# Revit family: Faucet-Kitchen-KOHLER-Ealing-K-R28702_1
name_source: partatom
category: Plumbing Fixtures
units: mm (PartAtom-declared; Revit-internal decimal feet)

## family parameters
Cut with Voids When Loaded = No
Host = Face
Maintain Annotation Orientation = No
OmniClass Number = 23.31.11.00
OmniClass Title = Faucets
Part Type = Normal
Room Calculation Point = No
Round Connector Dimension = Use Diameter
Shared = No

## types (6) — shared parameters
ADA Compliant = Yes
Assembly Code = D2010
CW Connection = Yes
Cold Water Inlet = Cold Water Inlet
Date Modified = 05/28/2022
Default Elevation = 36"
Description = Single-handle semi-professional kitchen sink faucet
Drain Included = No
Flow Rate = 2 GPM
HW Connection = Yes
Handle Clearance = 4"
Hot Water Inlet = Hot Water Inlet
Length = 9"
Manufacturer = Kohler Co.
Master Format 2014 = 22 41 39
Master Format 2014 Name = Residential Faucets, Supplies, and Trim
Material = Premium Metal Construction
Pressure = 60.00 psi
Product Documentation Link = https://www.us.kohler.com
Product Name = Ealing
Product Page URL = http://www.us.kohler.com
Spout Reach = 9"
URL = https://www.us.kohler.com
Vent Connection = No
Waste Connection = No
Waste Water Outlet = Waste Water Outlet
WaterSense Certified = No

## per-type parameters (varying)
| type | Finish | Hose Material | Model | Secondary Material | Type |
| 2BZ-Elegant Black | Kohler-Metal-2BZ-Elegant_Black | Kohler-Plastic-58-Thunder_Grey | K-R28702-SD-2BZ | Kohler-Plastic-58-Thunder_Grey | 1 |
| 2MB-Vibrant Brushed Moderne Brass | Kohler-Metal-2MB-Vibrant_Brushed_Moderne_Brass | Kohler-Plastic-58-Thunder_Grey | K-R28702-SD-2MB | Kohler-Plastic-58-Thunder_Grey | 2 |
| BL-Matte Black | Kohler-Metal-BL-Matte_Black | Kohler-Plastic-58-Thunder_Grey | K-R28702-SD-BL | Kohler-Plastic-58-Thunder_Grey | 3 |
| BN-Vibrant Brushed Nickel | Kohler-Metal-BN-Vibrant_Brushed_Nickel | Kohler-Plastic-58-Thunder_Grey | K-R28702-SD-BN | Kohler-Metal-BN-Vibrant_Brushed_Nickel | 4 |
| CP-Polished Chrome | Kohler-Metal-CP-Polished_Chrome | Kohler-Plastic-58-Thunder_Grey | K-R28702-SD-CP | Kohler-Metal-CP-Polished_Chrome | 5 |
| VS-Vibrant Stainless | Kohler-Metal-VS-Vibrant_Stainless | Kohler-Plastic-95-Ice_Grey | K-R28702-SD-VS | Kohler-Metal-VS-Vibrant_Stainless | 6 |

## geometry (parser evidence)
native form markers: Sweep x9
no freeform markers — native parametric forms only
